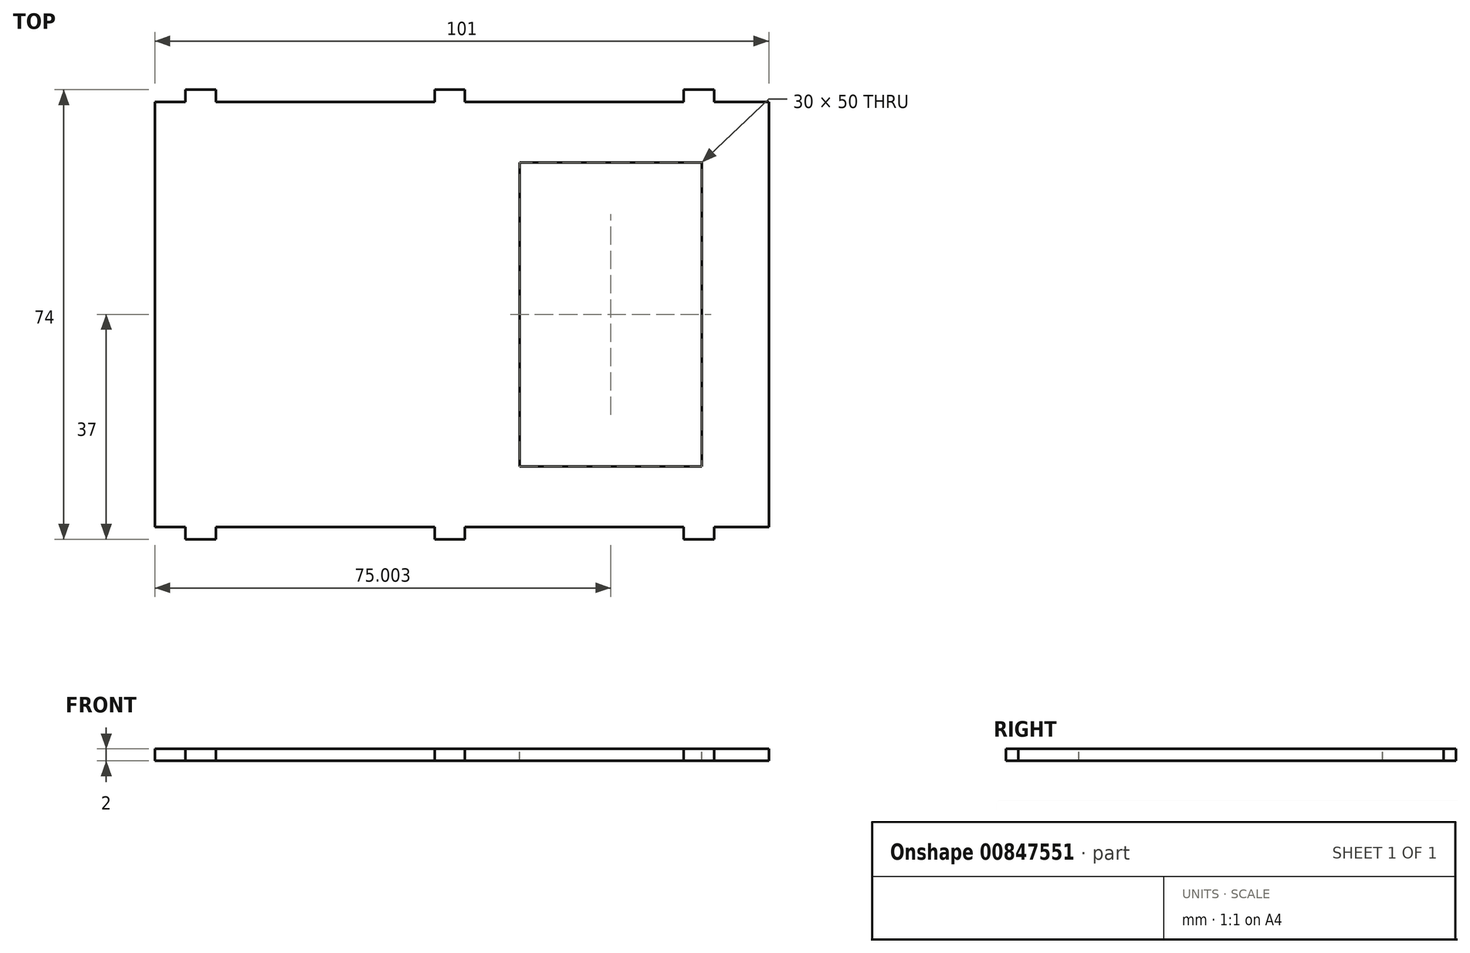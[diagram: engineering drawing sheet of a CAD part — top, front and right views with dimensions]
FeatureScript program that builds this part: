
annotation { "Feature Type Name" : "Feature", "Feature Type Description" : "" }
export const myFeature = defineFeature(function(context is Context, id is Id, definition is map)
    precondition{}
    {
        {
            var Q0;
            Q0=qCreatedBy(makeId("Top.planeOp"),FACE);
            var sketch = newSketch(context, id + "F0", { "sketchPlane" : qUnion([Q0])});
            skLineSegment(sketch, "E0.bottom", {"start": v(-42.38, 28.9) * mm, "end": v(58.62, 28.9) * mm});
            skLineSegment(sketch, "E0.top", {"start": v(-42.38, -41.1) * mm, "end": v(58.62, -41.1) * mm});
            skLineSegment(sketch, "E0.left", {"start": v(-42.38, 28.9) * mm, "end": v(-42.38, -41.1) * mm});
            skLineSegment(sketch, "E0.right", {"start": v(58.62, 28.9) * mm, "end": v(58.62, -41.1) * mm});
            skLineSegment(sketch, "E1.left", {"start": v(-42.38, 28.9) * mm, "end": v(-42.38, 28.9) * mm});
            skLineSegment(sketch, "E1.right", {"start": v(58.62, 28.9) * mm, "end": v(58.62, 28.9) * mm});
            skLineSegment(sketch, "E2.top", {"start": v(-42.38, 30.9) * mm, "end": v(58.62, 30.9) * mm});
            skLineSegment(sketch, "E2.left", {"start": v(-42.38, 28.9) * mm, "end": v(-42.38, 30.9) * mm});
            skLineSegment(sketch, "E2.right", {"start": v(58.62, 28.9) * mm, "end": v(58.62, 30.9) * mm});
            skLineSegment(sketch, "E3.top", {"start": v(-42.38, -43.1) * mm, "end": v(58.62, -43.1) * mm});
            skLineSegment(sketch, "E3.left", {"start": v(-42.38, -41.1) * mm, "end": v(-42.38, -43.1) * mm});
            skLineSegment(sketch, "E3.right", {"start": v(58.62, -41.1) * mm, "end": v(58.62, -43.1) * mm});
            skLineSegment(sketch, "E4.bottom", {"start": v(-42.38, 30.9) * mm, "end": v(-44.38, 30.9) * mm});
            skLineSegment(sketch, "E4.top", {"start": v(-42.38, -43.1) * mm, "end": v(-44.38, -43.1) * mm});
            skLineSegment(sketch, "E4.left", {"start": v(-42.38, 30.9) * mm, "end": v(-42.38, -43.1) * mm});
            skLineSegment(sketch, "E4.right", {"start": v(-44.38, 30.9) * mm, "end": v(-44.38, -43.1) * mm});
            skLineSegment(sketch, "E5.bottom", {"start": v(58.62, 30.9) * mm, "end": v(60.62, 30.9) * mm});
            skLineSegment(sketch, "E5.top", {"start": v(58.62, -43.1) * mm, "end": v(60.62, -43.1) * mm});
            skLineSegment(sketch, "E5.left", {"start": v(58.62, 30.9) * mm, "end": v(58.62, -43.1) * mm});
            skLineSegment(sketch, "E5.right", {"start": v(60.62, 30.9) * mm, "end": v(60.62, -43.1) * mm});
            skSolve(sketch);
        }
        {
            var Q0;
            Q0=makeQuery(id+"F0.imprint","IMPRINT",FACE,{"disambiguationData":[TD([[makeQuery(id+"F0.imprint","IMPRINT",EDGE,{"derivedFrom":sQuery(id+"F0.wireOp",EDGE,"E0.left")}),-1.0]])]});
            var Q1;
            Q1=makeQuery(id+"F0.imprint","IMPRINT",FACE,{"disambiguationData":[TD([[makeQuery(id+"F0.imprint","IMPRINT",EDGE,{"derivedFrom":sQuery(id+"F0.wireOp",EDGE,"E0.bottom")}),1.0]])]});
            var Q2;
            Q2=makeQuery(id+"F0.imprint","IMPRINT",FACE,{"disambiguationData":[TD([[makeQuery(id+"F0.imprint","IMPRINT",EDGE,{"derivedFrom":sQuery(id+"F0.wireOp",EDGE,"E0.right")}),1.0]])]});
            var Q3;
            Q3=makeQuery(id+"F0.imprint","IMPRINT",FACE,{"disambiguationData":[TD([[makeQuery(id+"F0.imprint","IMPRINT",EDGE,{"derivedFrom":sQuery(id+"F0.wireOp",EDGE,"E0.top")}),-1.0]])]});
            extrude(context, id + "F1", {"entities" : qUnion([Q0, Q1, Q2, Q3]), "depth" : 12 * mm, "offsetDistance" : 25 * mm});
        }
        {
            var Q0;
            Q0=makeQuery(id+"F0.imprint","IMPRINT",FACE,{"disambiguationData":[TD([[makeQuery(id+"F0.imprint","IMPRINT",EDGE,{"derivedFrom":sQuery(id+"F0.wireOp",EDGE,"E0.bottom")}),-1.0]])]});
            extrude(context, id + "F2", {"entities" : qUnion([Q0]), "operationType" : NewBodyOperationType.ADD, "depth" : 2 * mm, "offsetDistance" : 25 * mm});
        }
        {
            var Q0;
            Q0=makeQuery(id+"F1.opExtrude","SWEPT_FACE",FACE,{"disambiguationData":[OSD([sQuery(id+"F0.wireOp",EDGE,"E5.right")])]});
            var sketch = newSketch(context, id + "F3", { "sketchPlane" : qUnion([Q0])});
            skLineSegment(sketch, "E6.bottom", {"start": v(-35.1, 0) * mm, "end": v(12.9, 0) * mm});
            skLineSegment(sketch, "E6.top", {"start": v(-35.1, 12) * mm, "end": v(12.9, 12) * mm});
            skLineSegment(sketch, "E6.left", {"start": v(-35.1, 0) * mm, "end": v(-35.1, 12) * mm});
            skLineSegment(sketch, "E6.right", {"start": v(12.9, 0) * mm, "end": v(12.9, 12) * mm});
            skSolve(sketch);
        }
        {
            var Q0;
            Q0=makeQuery(id+"F1.opExtrude","SWEPT_FACE",FACE,{"disambiguationData":[OSD([sQuery(id+"F0.wireOp",EDGE,"E3.top"),sQuery(id+"F0.wireOp",EDGE,"E4.top"),sQuery(id+"F0.wireOp",EDGE,"E5.top")])]});
            var sketch = newSketch(context, id + "F4", { "sketchPlane" : qUnion([Q0])});
            skCircle(sketch, "E7", {"center": v(44.62, 5) * mm, "radius": 1.75 * mm});
            skCircle(sketch, "E8.1.0.0", {"center": v(-32.38, 5) * mm, "radius": 1.75 * mm});
            skLineSegment(sketch, "E8.direction1", {"start": v(44.62, 5) * mm, "end": v(-32.38, 5) * mm, "construction": true});
            skSolve(sketch);
        }
        {
            var Q0;
            Q0=makeQuery(id+"F4.imprint","IMPRINT",FACE,{"disambiguationData":[TD([[makeQuery(id+"F4.imprint","IMPRINT",EDGE,{"derivedFrom":sQuery(id+"F4.wireOp",EDGE,"E7")}),1.0]])]});
            var Q1;
            Q1=makeQuery(id+"F4.imprint","IMPRINT",FACE,{"disambiguationData":[TD([[makeQuery(id+"F4.imprint","IMPRINT",EDGE,{"derivedFrom":sQuery(id+"F4.wireOp",EDGE,"E8.1.0.0")}),1.0]])]});
            extrude(context, id + "F5", {"entities" : qUnion([Q0, Q1]), "operationType" : NewBodyOperationType.REMOVE, "oppositeDirection" : true, "depth" : 100 * mm, "offsetDistance" : 25 * mm});
        }
        {
            var Q0;
            {var subQ0=sQuery(id+"F3.wireOp",EDGE,"E6.top");Q0=makeQuery(id+"F3.imprint","IMPRINT",FACE,{"disambiguationData":[TD([[makeQuery(id+"F3.imprint","IMPRINT",EDGE,{"derivedFrom":subQ0}),-1.0]])]});}
            var Q1;
            {var subQ0=sQuery(id+"F3.wireOp",EDGE,"E6.bottom");Q1=makeQuery(id+"F3.imprint","IMPRINT",FACE,{"disambiguationData":[TD([[makeQuery(id+"F3.imprint","IMPRINT",EDGE,{"derivedFrom":subQ0}),-1.0]])]});}
            extrude(context, id + "F6", {"entities" : qUnion([Q0, Q1]), "operationType" : NewBodyOperationType.REMOVE, "oppositeDirection" : true, "depth" : 2 * mm, "offsetDistance" : 25 * mm});
        }
        {
            var Q0;
            Q0=makeQuery(id+"F2.opExtrude","CAP_FACE",FACE,{"disambiguationData":[OSD([sQuery(id+"F0.wireOp",EDGE,"E0.bottom"),sQuery(id+"F0.wireOp",EDGE,"E0.top"),sQuery(id+"F0.wireOp",EDGE,"E0.left"),sQuery(id+"F0.wireOp",EDGE,"E0.right")])],"isStart":false});
            var sketch = newSketch(context, id + "F7", { "sketchPlane" : qUnion([Q0])});
            skLineSegment(sketch, "E9.bottom", {"start": v(-32.38, -31.1) * mm, "end": v(47.62, -31.1) * mm});
            skLineSegment(sketch, "E9.top", {"start": v(-32.38, 18.9) * mm, "end": v(47.62, 18.9) * mm});
            skLineSegment(sketch, "E9.left", {"start": v(2.62, -31.1) * mm, "end": v(2.62, 18.9) * mm});
            skLineSegment(sketch, "E9.right", {"start": v(47.62, -31.1) * mm, "end": v(47.62, 18.9) * mm});
            skLineSegment(sketch, "E10.bottom", {"start": v(2.62, 18.9) * mm, "end": v(17.62, 18.9) * mm});
            skLineSegment(sketch, "E10.top", {"start": v(2.62, -31.1) * mm, "end": v(17.62, -31.1) * mm});
            skLineSegment(sketch, "E10.left", {"start": v(2.62, 18.9) * mm, "end": v(2.62, -31.1) * mm});
            skLineSegment(sketch, "E10.right", {"start": v(17.62, 18.9) * mm, "end": v(17.62, -31.1) * mm});
            skLineSegment(sketch, "E11", {"start": v(-32.38, 18.9) * mm, "end": v(-32.38, -31.1) * mm});
            skSolve(sketch);
        }
        {
            var Q0;
            {var subQ2=sQuery(id+"F7.wireOp",EDGE,"E10.left");Q0=makeQuery(id+"F7.imprint","IMPRINT",FACE,{"disambiguationData":[TD([[makeQuery(id+"F7.imprint","IMPRINT",EDGE,{"derivedFrom":subQ2}),-1.0]])]});}
            var Q1;
            {var subQ0=sQuery(id+"F7.wireOp",EDGE,"E9.right");Q1=makeQuery(id+"F7.imprint","IMPRINT",FACE,{"disambiguationData":[TD([[makeQuery(id+"F7.imprint","IMPRINT",EDGE,{"derivedFrom":subQ0}),1.0]])]});}
            extrude(context, id + "F8", {"entities" : qUnion([Q0, Q1]), "operationType" : NewBodyOperationType.REMOVE, "oppositeDirection" : true, "depth" : 2 * mm, "offsetDistance" : 25 * mm});
        }
        {
            var Q0;
            Q0=makeQuery(id+"F4.imprint","IMPRINT",FACE,{"disambiguationData":[TD([[makeQuery(id+"F4.imprint","IMPRINT",EDGE,{"derivedFrom":sQuery(id+"F4.wireOp",EDGE,"E7")}),-1.0]])]});
            var sketch = newSketch(context, id + "F9", { "sketchPlane" : qUnion([Q0])});
            skLineSegment(sketch, "E12.bottom", {"start": v(-37.38, 2) * mm, "end": v(-32.38, 2) * mm});
            skLineSegment(sketch, "E12.top", {"start": v(-37.38, 12) * mm, "end": v(-32.38, 12) * mm});
            skLineSegment(sketch, "E12.left", {"start": v(-37.38, 2) * mm, "end": v(-37.38, 12) * mm});
            skLineSegment(sketch, "E12.right", {"start": v(-32.38, 2) * mm, "end": v(-32.38, 12) * mm});
            skLineSegment(sketch, "E13.1.0.0", {"start": v(3.62, 12) * mm, "end": v(8.62, 12) * mm});
            skLineSegment(sketch, "E13.1.0.1", {"start": v(3.62, 2) * mm, "end": v(8.62, 2) * mm});
            skLineSegment(sketch, "E13.1.0.2", {"start": v(8.62, 2) * mm, "end": v(8.62, 12) * mm});
            skLineSegment(sketch, "E13.1.0.3", {"start": v(3.62, 2) * mm, "end": v(3.62, 12) * mm});
            skLineSegment(sketch, "E13.2.0.0", {"start": v(44.62, 12) * mm, "end": v(49.62, 12) * mm});
            skLineSegment(sketch, "E13.2.0.1", {"start": v(44.62, 2) * mm, "end": v(49.62, 2) * mm});
            skLineSegment(sketch, "E13.2.0.2", {"start": v(49.62, 2) * mm, "end": v(49.62, 12) * mm});
            skLineSegment(sketch, "E13.2.0.3", {"start": v(44.62, 2) * mm, "end": v(44.62, 12) * mm});
            skSolve(sketch);
        }
        {
            var Q0;
            Q0 = qSketchRegion(id + "F9", true);
            extrude(context, id + "F10", {"entities" : qUnion([Q0]), "operationType" : NewBodyOperationType.REMOVE, "oppositeDirection" : true, "depth" : 80 * mm, "offsetDistance" : 25 * mm});
        }
        {
            var Q0;
            {var subQ0=sQuery(id+"F0.wireOp",EDGE,"E0.bottom");var subQ1=sQuery(id+"F0.wireOp",EDGE,"E5.bottom");var subQ2=sQuery(id+"F0.wireOp",EDGE,"E4.bottom");var subQ3=sQuery(id+"F0.wireOp",EDGE,"E2.top");Q0=makeQuery(id+"F10.boolean.opBoolean","SPLIT",FACE,{"disambiguationData":[TD([makeQuery(id+"F1.opExtrude","SWEPT_FACE",FACE,{"disambiguationData":[OSD([subQ0])]}),makeQuery(id+"F1.opExtrude","SWEPT_FACE",FACE,{"disambiguationData":[OSD([subQ3,subQ2,subQ1])]}),makeQuery(id+"F10.opExtrude","SWEPT_FACE",FACE,{"disambiguationData":[OSD([sQuery(id+"F9.wireOp",EDGE,"E12.right")])]}),makeQuery(id+"F10.opExtrude","SWEPT_FACE",FACE,{"disambiguationData":[OSD([sQuery(id+"F9.wireOp",EDGE,"E13.1.0.3")])]})])],"derivedFrom":makeQuery(id+"F1.opExtrude","CAP_FACE",FACE,{"disambiguationData":[OSD([subQ0,sQuery(id+"F0.wireOp",EDGE,"E0.top"),sQuery(id+"F0.wireOp",EDGE,"E0.left"),sQuery(id+"F0.wireOp",EDGE,"E0.right"),subQ3,sQuery(id+"F0.wireOp",EDGE,"E3.top"),subQ2,sQuery(id+"F0.wireOp",EDGE,"E4.top"),sQuery(id+"F0.wireOp",EDGE,"E4.right"),subQ1,sQuery(id+"F0.wireOp",EDGE,"E5.top"),sQuery(id+"F0.wireOp",EDGE,"E5.right")])],"isStart":false})});}
            var Q1;
            {var subQ0=sQuery(id+"F0.wireOp",EDGE,"E0.bottom");var subQ1=sQuery(id+"F0.wireOp",EDGE,"E5.bottom");var subQ2=sQuery(id+"F0.wireOp",EDGE,"E4.bottom");var subQ3=sQuery(id+"F0.wireOp",EDGE,"E2.top");Q1=makeQuery(id+"F10.boolean.opBoolean","SPLIT",FACE,{"disambiguationData":[TD([makeQuery(id+"F1.opExtrude","SWEPT_FACE",FACE,{"disambiguationData":[OSD([subQ0])]}),makeQuery(id+"F1.opExtrude","SWEPT_FACE",FACE,{"disambiguationData":[OSD([subQ3,subQ2,subQ1])]}),makeQuery(id+"F10.opExtrude","SWEPT_FACE",FACE,{"disambiguationData":[OSD([sQuery(id+"F9.wireOp",EDGE,"E13.1.0.2")])]}),makeQuery(id+"F10.opExtrude","SWEPT_FACE",FACE,{"disambiguationData":[OSD([sQuery(id+"F9.wireOp",EDGE,"E13.2.0.3")])]})])],"derivedFrom":makeQuery(id+"F1.opExtrude","CAP_FACE",FACE,{"disambiguationData":[OSD([subQ0,sQuery(id+"F0.wireOp",EDGE,"E0.top"),sQuery(id+"F0.wireOp",EDGE,"E0.left"),sQuery(id+"F0.wireOp",EDGE,"E0.right"),subQ3,sQuery(id+"F0.wireOp",EDGE,"E3.top"),subQ2,sQuery(id+"F0.wireOp",EDGE,"E4.top"),sQuery(id+"F0.wireOp",EDGE,"E4.right"),subQ1,sQuery(id+"F0.wireOp",EDGE,"E5.top"),sQuery(id+"F0.wireOp",EDGE,"E5.right")])],"isStart":false})});}
            var Q2;
            {var subQ0=sQuery(id+"F0.wireOp",EDGE,"E5.right");var subQ1=sQuery(id+"F0.wireOp",EDGE,"E5.bottom");var subQ2=sQuery(id+"F0.wireOp",EDGE,"E4.bottom");var subQ3=sQuery(id+"F0.wireOp",EDGE,"E2.top");var subQ4=sQuery(id+"F0.wireOp",EDGE,"E0.right");var subQ5=sQuery(id+"F0.wireOp",EDGE,"E0.bottom");Q2=makeQuery(id+"F10.boolean.opBoolean","SPLIT",FACE,{"disambiguationData":[TD([makeQuery(id+"F1.opExtrude","SWEPT_FACE",FACE,{"disambiguationData":[OSD([subQ5])]}),makeQuery(id+"F1.opExtrude","SWEPT_FACE",FACE,{"disambiguationData":[OSD([subQ4])]}),makeQuery(id+"F1.opExtrude","SWEPT_FACE",FACE,{"disambiguationData":[OSD([subQ3,subQ2,subQ1])]}),makeQuery(id+"F1.opExtrude","SWEPT_FACE",FACE,{"disambiguationData":[OSD([subQ0])]}),makeQuery(id+"F6.boolean.opBoolean","COPY",FACE,{"derivedFrom":makeQuery(id+"F6.opExtrude","SWEPT_FACE",FACE,{"disambiguationData":[OSD([sQuery(id+"F3.wireOp",EDGE,"E6.right")])]})}),makeQuery(id+"F10.opExtrude","SWEPT_FACE",FACE,{"disambiguationData":[OSD([sQuery(id+"F9.wireOp",EDGE,"E13.2.0.2")])]})])],"derivedFrom":makeQuery(id+"F1.opExtrude","CAP_FACE",FACE,{"disambiguationData":[OSD([subQ5,sQuery(id+"F0.wireOp",EDGE,"E0.top"),sQuery(id+"F0.wireOp",EDGE,"E0.left"),subQ4,subQ3,sQuery(id+"F0.wireOp",EDGE,"E3.top"),subQ2,sQuery(id+"F0.wireOp",EDGE,"E4.top"),sQuery(id+"F0.wireOp",EDGE,"E4.right"),subQ1,sQuery(id+"F0.wireOp",EDGE,"E5.top"),subQ0])],"isStart":false})});}
            var Q3;
            {var subQ0=sQuery(id+"F0.wireOp",EDGE,"E5.right");var subQ1=sQuery(id+"F0.wireOp",EDGE,"E5.top");var subQ2=sQuery(id+"F0.wireOp",EDGE,"E4.top");var subQ3=sQuery(id+"F0.wireOp",EDGE,"E3.top");var subQ4=sQuery(id+"F0.wireOp",EDGE,"E0.right");var subQ5=sQuery(id+"F0.wireOp",EDGE,"E0.top");Q3=makeQuery(id+"F10.boolean.opBoolean","SPLIT",FACE,{"disambiguationData":[TD([makeQuery(id+"F1.opExtrude","SWEPT_FACE",FACE,{"disambiguationData":[OSD([subQ5])]}),makeQuery(id+"F1.opExtrude","SWEPT_FACE",FACE,{"disambiguationData":[OSD([subQ4])]}),makeQuery(id+"F1.opExtrude","SWEPT_FACE",FACE,{"disambiguationData":[OSD([subQ3,subQ2,subQ1])]}),makeQuery(id+"F1.opExtrude","SWEPT_FACE",FACE,{"disambiguationData":[OSD([subQ0])]}),makeQuery(id+"F6.boolean.opBoolean","COPY",FACE,{"derivedFrom":makeQuery(id+"F6.opExtrude","SWEPT_FACE",FACE,{"disambiguationData":[OSD([sQuery(id+"F3.wireOp",EDGE,"E6.left")])]})}),makeQuery(id+"F10.opExtrude","SWEPT_FACE",FACE,{"disambiguationData":[OSD([sQuery(id+"F9.wireOp",EDGE,"E13.2.0.2")])]})])],"derivedFrom":makeQuery(id+"F1.opExtrude","CAP_FACE",FACE,{"disambiguationData":[OSD([sQuery(id+"F0.wireOp",EDGE,"E0.bottom"),subQ5,sQuery(id+"F0.wireOp",EDGE,"E0.left"),subQ4,sQuery(id+"F0.wireOp",EDGE,"E2.top"),subQ3,sQuery(id+"F0.wireOp",EDGE,"E4.bottom"),subQ2,sQuery(id+"F0.wireOp",EDGE,"E4.right"),sQuery(id+"F0.wireOp",EDGE,"E5.bottom"),subQ1,subQ0])],"isStart":false})});}
            var Q4;
            {var subQ0=sQuery(id+"F0.wireOp",EDGE,"E0.top");var subQ1=sQuery(id+"F0.wireOp",EDGE,"E5.top");var subQ2=sQuery(id+"F0.wireOp",EDGE,"E4.top");var subQ3=sQuery(id+"F0.wireOp",EDGE,"E3.top");Q4=makeQuery(id+"F10.boolean.opBoolean","SPLIT",FACE,{"disambiguationData":[TD([makeQuery(id+"F1.opExtrude","SWEPT_FACE",FACE,{"disambiguationData":[OSD([subQ0])]}),makeQuery(id+"F1.opExtrude","SWEPT_FACE",FACE,{"disambiguationData":[OSD([subQ3,subQ2,subQ1])]}),makeQuery(id+"F10.opExtrude","SWEPT_FACE",FACE,{"disambiguationData":[OSD([sQuery(id+"F9.wireOp",EDGE,"E13.1.0.2")])]}),makeQuery(id+"F10.opExtrude","SWEPT_FACE",FACE,{"disambiguationData":[OSD([sQuery(id+"F9.wireOp",EDGE,"E13.2.0.3")])]})])],"derivedFrom":makeQuery(id+"F1.opExtrude","CAP_FACE",FACE,{"disambiguationData":[OSD([sQuery(id+"F0.wireOp",EDGE,"E0.bottom"),subQ0,sQuery(id+"F0.wireOp",EDGE,"E0.left"),sQuery(id+"F0.wireOp",EDGE,"E0.right"),sQuery(id+"F0.wireOp",EDGE,"E2.top"),subQ3,sQuery(id+"F0.wireOp",EDGE,"E4.bottom"),subQ2,sQuery(id+"F0.wireOp",EDGE,"E4.right"),sQuery(id+"F0.wireOp",EDGE,"E5.bottom"),subQ1,sQuery(id+"F0.wireOp",EDGE,"E5.right")])],"isStart":false})});}
            var Q5;
            {var subQ0=sQuery(id+"F0.wireOp",EDGE,"E0.top");var subQ1=sQuery(id+"F0.wireOp",EDGE,"E5.top");var subQ2=sQuery(id+"F0.wireOp",EDGE,"E4.top");var subQ3=sQuery(id+"F0.wireOp",EDGE,"E3.top");Q5=makeQuery(id+"F10.boolean.opBoolean","SPLIT",FACE,{"disambiguationData":[TD([makeQuery(id+"F1.opExtrude","SWEPT_FACE",FACE,{"disambiguationData":[OSD([subQ0])]}),makeQuery(id+"F1.opExtrude","SWEPT_FACE",FACE,{"disambiguationData":[OSD([subQ3,subQ2,subQ1])]}),makeQuery(id+"F10.opExtrude","SWEPT_FACE",FACE,{"disambiguationData":[OSD([sQuery(id+"F9.wireOp",EDGE,"E12.right")])]}),makeQuery(id+"F10.opExtrude","SWEPT_FACE",FACE,{"disambiguationData":[OSD([sQuery(id+"F9.wireOp",EDGE,"E13.1.0.3")])]})])],"derivedFrom":makeQuery(id+"F1.opExtrude","CAP_FACE",FACE,{"disambiguationData":[OSD([sQuery(id+"F0.wireOp",EDGE,"E0.bottom"),subQ0,sQuery(id+"F0.wireOp",EDGE,"E0.left"),sQuery(id+"F0.wireOp",EDGE,"E0.right"),sQuery(id+"F0.wireOp",EDGE,"E2.top"),subQ3,sQuery(id+"F0.wireOp",EDGE,"E4.bottom"),subQ2,sQuery(id+"F0.wireOp",EDGE,"E4.right"),sQuery(id+"F0.wireOp",EDGE,"E5.bottom"),subQ1,sQuery(id+"F0.wireOp",EDGE,"E5.right")])],"isStart":false})});}
            var Q6;
            {var subQ0=sQuery(id+"F0.wireOp",EDGE,"E5.bottom");var subQ1=sQuery(id+"F0.wireOp",EDGE,"E4.bottom");var subQ2=sQuery(id+"F0.wireOp",EDGE,"E2.top");var subQ3=sQuery(id+"F0.wireOp",EDGE,"E0.left");var subQ4=sQuery(id+"F0.wireOp",EDGE,"E0.top");var subQ5=sQuery(id+"F0.wireOp",EDGE,"E0.bottom");var subQ6=sQuery(id+"F0.wireOp",EDGE,"E5.top");var subQ7=sQuery(id+"F0.wireOp",EDGE,"E4.top");var subQ8=sQuery(id+"F0.wireOp",EDGE,"E3.top");var subQ9=sQuery(id+"F0.wireOp",EDGE,"E4.right");Q6=makeQuery(id+"F10.boolean.opBoolean","SPLIT",FACE,{"disambiguationData":[TD([makeQuery(id+"F1.opExtrude","SWEPT_FACE",FACE,{"disambiguationData":[OSD([subQ5])]}),makeQuery(id+"F1.opExtrude","SWEPT_FACE",FACE,{"disambiguationData":[OSD([subQ4])]}),makeQuery(id+"F1.opExtrude","SWEPT_FACE",FACE,{"disambiguationData":[OSD([subQ3])]}),makeQuery(id+"F1.opExtrude","SWEPT_FACE",FACE,{"disambiguationData":[OSD([subQ2,subQ1,subQ0])]}),makeQuery(id+"F1.opExtrude","SWEPT_FACE",FACE,{"disambiguationData":[OSD([subQ8,subQ7,subQ6])]}),makeQuery(id+"F1.opExtrude","SWEPT_FACE",FACE,{"disambiguationData":[OSD([subQ9])]}),makeQuery(id+"F10.opExtrude","SWEPT_FACE",FACE,{"disambiguationData":[OSD([sQuery(id+"F9.wireOp",EDGE,"E12.left")])]})])],"derivedFrom":makeQuery(id+"F1.opExtrude","CAP_FACE",FACE,{"disambiguationData":[OSD([subQ5,subQ4,subQ3,sQuery(id+"F0.wireOp",EDGE,"E0.right"),subQ2,subQ8,subQ1,subQ7,subQ9,subQ0,subQ6,sQuery(id+"F0.wireOp",EDGE,"E5.right")])],"isStart":false})});}
            extrude(context, id + "F11", {"entities" : qUnion([Q0, Q1, Q2, Q3, Q4, Q5, Q6]), "operationType" : NewBodyOperationType.REMOVE, "oppositeDirection" : true, "depth" : 12 * mm, "offsetDistance" : 25 * mm});
        }
    });
